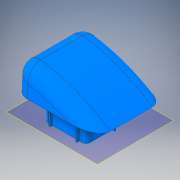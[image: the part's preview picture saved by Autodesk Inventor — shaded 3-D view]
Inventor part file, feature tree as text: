
AUTODESK INVENTOR PART (.ipt)
format: ipt  version: 2017 (Build 210142000, 142)  size: 397,824 bytes
history: native  units: in
note: dims shown in document units (in); Inventor stores cm internally (conversion verified against a paired STEP export)
features: extrude x2, sketch x2, fillet x1, shell x1, plane x1, projected_geometry x1
ambient origin geometry x8: Origin, YZ Plane, XZ Plane, XY Plane, X Axis, Y Axis, Z Axis, Center Point
bodies: Solid1 (feature_tree)
feature tree (8):
  extrude  "Extrusion1"  Depth=6.0in
  fillet  "Fillet1"  Radius=6.0in
  shell  "Shell1"  Thickness=0.64in
  plane  "Work Plane2"
  extrude  "Extrusion2"  Depth=0.4in
  sketch  "Sketch1"  dims[d0=3.04in d2=6.0in d6=6.0in d9=0.64in]
  sketch  "Sketch3"  dims[d10=3.01in d11=0.4in d12=2.55in d13=0.0in d14=0.5in d15=0.07in d36=0.67in d37=1.97in d38=0.68in d39=1.54in d40=0.29in d41=0.15in d42=0.05in d43=0.95in d44=1.94in d45=1.28in d46=0.09in d47=0.05in d48=0.025in d49=0.09in d50=0.05in d51=0.025in d52=0.09in d53=0.05in d54=0.025in d55=0.09in d56=0.025in d57=0.09in d58=0.05in d59=0.025in d60=0.09in d61=0.05in d62=0.025in d63=3.0in d64=0.0in]
  projected_geometry  "Projected Loop4"
